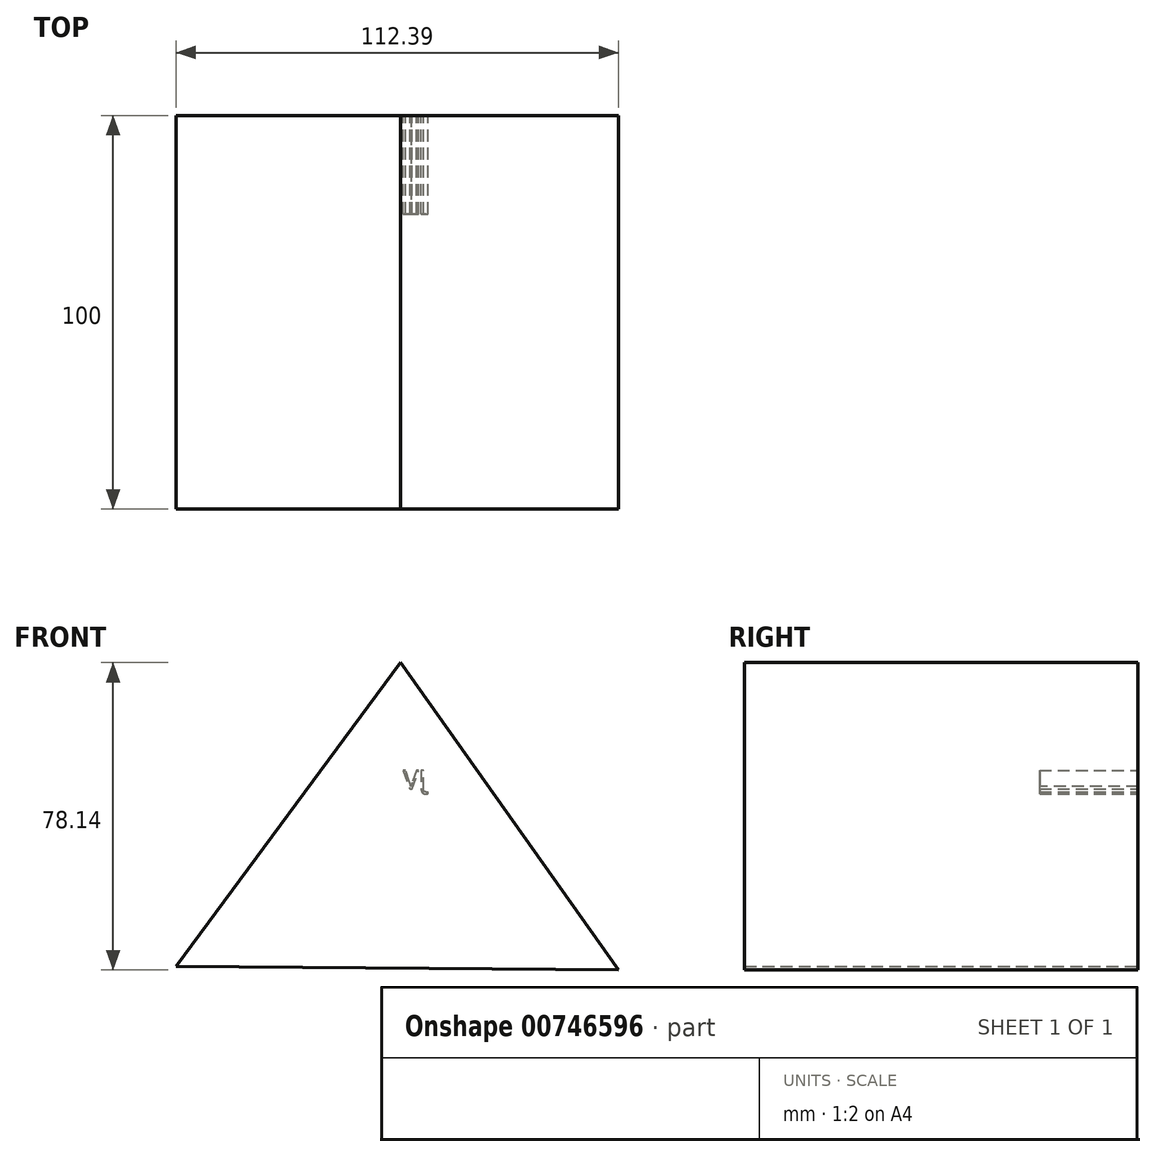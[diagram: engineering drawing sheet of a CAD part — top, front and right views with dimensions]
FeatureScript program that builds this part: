
annotation { "Feature Type Name" : "Feature", "Feature Type Description" : "" }
export const myFeature = defineFeature(function(context is Context, id is Id, definition is map)
    precondition{}
    {
        {
            var Q0;
            Q0=qCreatedBy(makeId("Front.planeOp"),FACE);
            var sketch = newSketch(context, id + "F0", { "sketchPlane" : qUnion([Q0])});
            skLineSegment(sketch, "E0", {"start": v(0, 53.35) * mm, "end": v(-56.96, -23.9) * mm});
            skLineSegment(sketch, "E1", {"start": v(0, 53.35) * mm, "end": v(55.43, -24.8) * mm});
            skLineSegment(sketch, "E2", {"start": v(-56.96, -23.9) * mm, "end": v(55.43, -24.8) * mm});
            skSolve(sketch);
        }
        {
            var Q0;
            Q0 = qSketchRegion(id + "F0", true);
            extrude(context, id + "F1", {"entities" : qUnion([Q0]), "depth" : 100 * mm, "offsetDistance" : 25 * mm});
        }
        {
            var Q0;
            Q0=makeQuery(id+"F1.opExtrude","CAP_FACE",FACE,{"disambiguationData":[OSD([sQuery(id+"F0.wireOp",EDGE,"E0"),sQuery(id+"F0.wireOp",EDGE,"E1"),sQuery(id+"F0.wireOp",EDGE,"E2")])],"isStart":true});
            var sketch = newSketch(context, id + "F2", { "sketchPlane" : qUnion([Q0])});
            skText(sketch, "E3", { "text": "JV", "fontName": "OpenSans-Regular.ttf"});
            const initialGuessF2  = {"E3": [-0.00646, 0.0212, 1, 0, 0.0048]};
            skSetInitialGuess(sketch, initialGuessF2);
            skSolve(sketch);
        }
        {
            var Q0;
            Q0 = qSketchRegion(id + "F2", true);
            extrude(context, id + "F3", {"entities" : qUnion([Q0]), "operationType" : NewBodyOperationType.REMOVE, "oppositeDirection" : true, "depth" : 25 * mm, "offsetDistance" : 25 * mm});
        }
    });
